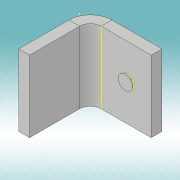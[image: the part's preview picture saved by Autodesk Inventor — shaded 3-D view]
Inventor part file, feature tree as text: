
AUTODESK INVENTOR PART (.ipt)
format: ipt  version: 2019 (Build 230136000, 136)  size: 137,216 bytes
history: native  units: mm
features: sketch x5, extrude x3, sheet_metal_op x3, other x1, projected_geometry x1
ambient origin geometry x8: Origin, YZ Plane, XZ Plane, XY Plane, X Axis, Y Axis, Z Axis, Center Point
bodies: Solid1 (feature_tree)
feature tree (13):
  extrude  "Extrusion1"  Depth=10.0mm
  sheet_metal_op  "Flange1"
  extrude  "Extrusion2"  Depth=1.5mm
  extrude  "Extrusion3"  Depth=1.5mm
  sketch  "Sketch5"  dims[d8=1.5mm d9=10.0mm d10=90.0deg d11=1.5mm d12=6.0mm d13=1.5mm d14=1.5mm d15=2.0mm d16=3.5mm d17=5.0mm d18=0.1mm d19=0.0mm d20=2.0mm d21=5.0mm d22=3.5mm d23=1.6mm d24=0.0mm]
  sketch  "Sketch1"  dims[d0=10.0mm d1=10.0mm]
  sketch  "Sketch2"  dims[d2=1.5mm d3=0.0mm d4=1.5mm]
  other  "Plate1"
  sheet_metal_op  "Bend1"
  sheet_metal_op  "Corner1"
  sketch  "Sketch3"  dims[d5=1.5mm d6=0.75mm]
  sketch  "Sketch4"  dims[d7=3.0mm]
  projected_geometry  "Projected Loop1"
